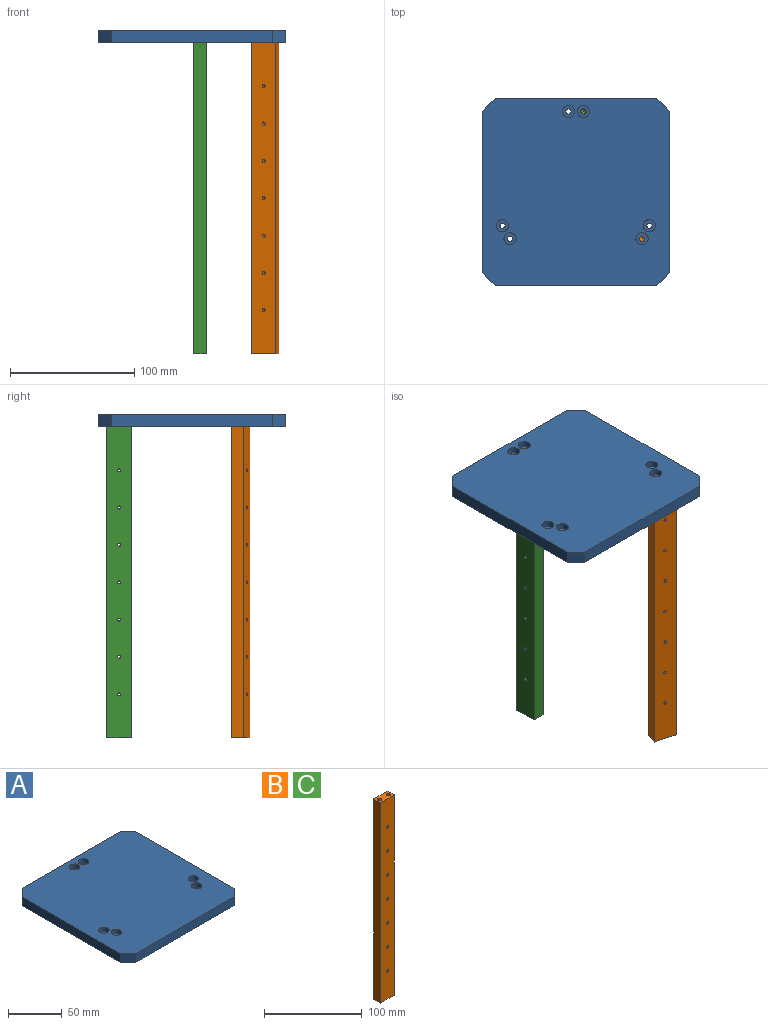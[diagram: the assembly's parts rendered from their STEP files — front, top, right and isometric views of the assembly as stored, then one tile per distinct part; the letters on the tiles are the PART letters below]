
ASSEMBLY  parts=3 mates=4
PART A: 28 faces, bbox 150x150x10 mm
  f0: plane 130x10mm, normal (-1,0,0), area 1300mm2, adj f4,f5,f24,f27
  f1: plane 130x10mm, normal (0,-1,0), area 1300mm2, adj f4,f5,f24,f25
  f2: plane 130x10mm, normal (1,0,0), area 1300mm2, adj f4,f5,f25,f26
  f3: plane 130x10mm, normal (0,1,0), area 1300mm2, adj f4,f5,f26,f27
  f4: plane 150x150mm, normal (0,0,1), area 21852mm2, adj f0,f1,f2,f3,f8,f11,f14,f17
  f5: plane 150x150mm, normal (0,0,-1), area 22216.9mm2, adj f0,f1,f2,f3,f6,f9,f12,f15
  f6: cylinder r=2.1mm len=5mm, axis (0,0,1), area 66mm2, adj f5,f7
  f7: plane 9.75x9.75mm, normal (0,0,1), area 60.8mm2, adj f6,f8
  f8: cylinder r=4.88mm len=9.75mm, axis (0,0,1), area 153.2mm2, adj f4,f7
  f9: cylinder r=2.1mm len=5mm, axis (0,0,1), area 66mm2, adj f5,f10
  f10: plane 9.75x9.75mm, normal (0,0,1), area 60.8mm2, adj f9,f11
  f11: cylinder r=4.88mm len=9.75mm, axis (0,0,1), area 153.2mm2, adj f4,f10
  f12: cylinder r=2.1mm len=5mm, axis (0,0,1), area 66mm2, adj f5,f13
  f13: plane 9.75x9.75mm, normal (0,0,1), area 60.8mm2, adj f12,f14
  f14: cylinder r=4.88mm len=9.75mm, axis (0,0,1), area 153.2mm2, adj f4,f13
  f15: cylinder r=2.1mm len=5mm, axis (0,0,1), area 66mm2, adj f5,f16
  f16: plane 9.75x9.75mm, normal (0,0,1), area 60.8mm2, adj f15,f17
  f17: cylinder r=4.88mm len=9.75mm, axis (0,0,1), area 153.2mm2, adj f4,f16
  f18: cylinder r=2.1mm len=5mm, axis (0,0,1), area 66mm2, adj f5,f19
  f19: plane 9.75x9.75mm, normal (0,0,1), area 60.8mm2, adj f18,f20
  f20: cylinder r=4.88mm len=9.75mm, axis (0,0,1), area 153.2mm2, adj f4,f19
  f21: cylinder r=2.1mm len=5mm, axis (0,0,1), area 66mm2, adj f5,f22
  f22: plane 9.75x9.75mm, normal (0,0,1), area 60.8mm2, adj f21,f23
  f23: cylinder r=4.88mm len=9.75mm, axis (0,0,1), area 153.2mm2, adj f4,f22
  f24: plane 10x10mm, normal (-0.71,-0.71,0), area 141.4mm2, adj f0,f1,f4,f5
  f25: plane 10x10mm, normal (0.71,-0.71,0), area 141.4mm2, adj f1,f2,f4,f5
  f26: plane 10x10mm, normal (0.71,0.71,0), area 141.4mm2, adj f2,f3,f4,f5
  f27: plane 10x10mm, normal (-0.71,0.71,0), area 141.4mm2, adj f0,f3,f4,f5
PART B: 21 faces, bbox 20x10x250 mm
  f0: plane 250x10mm, normal (-1,0,0), area 2500mm2, adj f1,f3,f4,f5
  f1: plane 20x10mm, normal (0,0,-1), area 172.3mm2, adj f0,f2,f4,f5,f6,f8
  f2: plane 250x10mm, normal (1,0,0), area 2500mm2, adj f1,f3,f4,f5
  f3: plane 20x10mm, normal (0,0,1), area 172.3mm2, adj f0,f2,f4,f5,f10,f12
  f4: plane 250x20mm, normal (0,-1,0), area 4965.6mm2, adj f0,f1,f2,f3,f14,f15,f16,f17
  f5: plane 250x20mm, normal (0,1,0), area 4965.6mm2, adj f0,f1,f2,f3,f14,f15,f16,f17
  f6: cylinder r=2.1mm len=15.8mm, axis (0,0,-1), area 208.5mm2, adj f1,f7
  f7: cone r=0mm half-angle=59deg, axis (0,0,-1), area 16.2mm2, adj f6
  f8: cylinder r=2.1mm len=15.8mm, axis (0,0,-1), area 208.5mm2, adj f1,f9
  f9: cone r=0mm half-angle=59deg, axis (0,0,-1), area 16.2mm2, adj f8
  f10: cylinder r=2.1mm len=15.8mm, axis (0,0,1), area 208.5mm2, adj f3,f11
  f11: cone r=0mm half-angle=59deg, axis (0,0,1), area 16.2mm2, adj f10
  f12: cylinder r=2.1mm len=15.8mm, axis (0,0,1), area 208.5mm2, adj f3,f13
  f13: cone r=0mm half-angle=59deg, axis (0,0,1), area 16.2mm2, adj f12
  f14: cylinder r=1.25mm len=10mm, axis (0,1,0), area 78.5mm2, adj f4,f5
  f15: cylinder r=1.25mm len=10mm, axis (0,1,0), area 78.5mm2, adj f4,f5
  f16: cylinder r=1.25mm len=10mm, axis (0,1,0), area 78.5mm2, adj f4,f5
  f17: cylinder r=1.25mm len=10mm, axis (0,1,0), area 78.5mm2, adj f4,f5
  f18: cylinder r=1.25mm len=10mm, axis (0,1,0), area 78.5mm2, adj f4,f5
  f19: cylinder r=1.25mm len=10mm, axis (0,1,0), area 78.5mm2, adj f4,f5
  f20: cylinder r=1.25mm len=10mm, axis (0,1,0), area 78.5mm2, adj f4,f5
PART C: same geometry as B
PLACE A t=(-61.01,-23.41,12.72)mm fixed
PLACE B rot(axis=(-0.99,0.13,0),180deg) t=(-3.48,-67.36,-112.28)mm
PLACE C rot(axis=(0,0,1),91.5deg) t=(-59.86,35.19,-112.28)mm
MATE ball C.f13 <-> A.f9  axis (0,0,1) through (-55.01,41.31,12.72)mm
MATE revolute B.f7 <-> A.f18  axis (0,0,1) through (-7.96,-60.97,12.72)mm
MATE planar C.f11 <-> A.f5  axis (0,0,1) through (-54.71,29.32,12.72)mm
MATE planar B.f3 <-> A.f5  axis (0,0,-1) through (-2.17,-62.53,-237.28)mm
